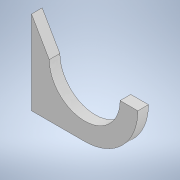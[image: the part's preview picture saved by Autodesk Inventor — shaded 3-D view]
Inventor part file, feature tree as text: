
AUTODESK INVENTOR PART (.ipt)
format: ipt  version: 2020.2 (Build 242310000, 310)  size: 112,128 bytes
history: native  units: in
note: dims shown in document units (in); Inventor stores cm internally (conversion verified against a paired STEP export)
features: extrude x2, sketch x2
ambient origin geometry x8: Origin, YZ Plane, XZ Plane, XY Plane, X Axis, Y Axis, Z Axis, Center Point
bodies: Solid1 (feature_tree)
feature tree (4):
  extrude  "Extrusion1"  Depth=1.0in
  extrude  "Extrusion2"  TaperAngle=60.0deg  [1 undecoded]
  sketch  "Sketch1"  dims[d0=1.5in d1=1.0in]
  sketch  "Sketch2"  dims[d2=0.15in d3=0.0in d5=60.0deg d6=0.15in d7=0.0in]
note: 1 required parameter value undecoded (feature->parameter linkage not recoverable at this tier; creation-order binding heuristic only, values carry confidence <= 0.55)
